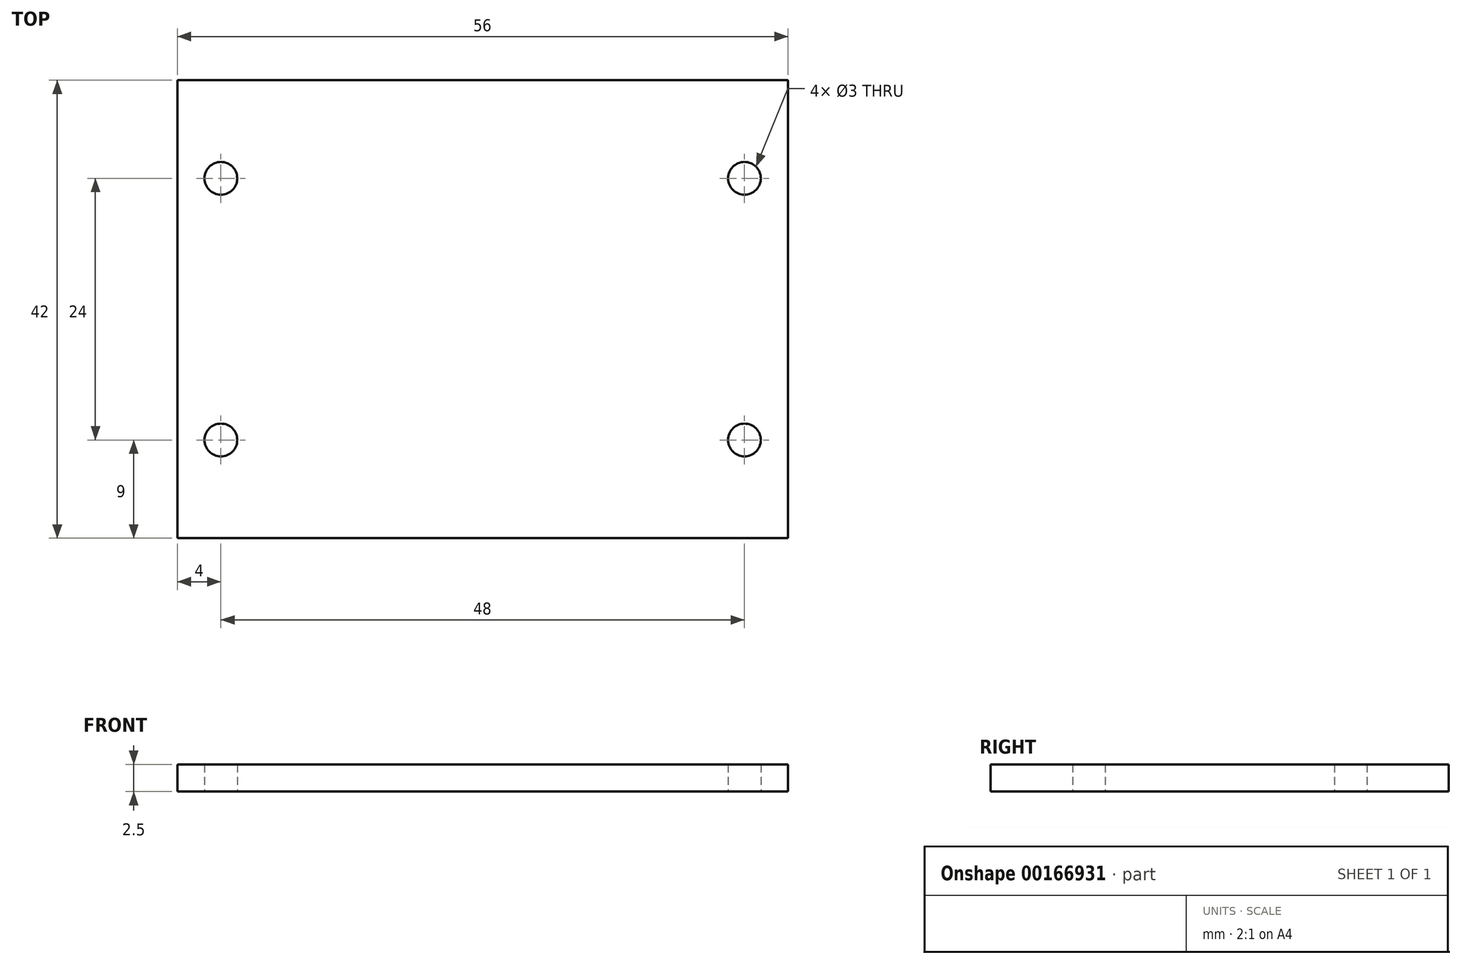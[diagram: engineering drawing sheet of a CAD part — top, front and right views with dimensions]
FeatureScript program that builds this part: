
annotation { "Feature Type Name" : "Feature", "Feature Type Description" : "" }
export const myFeature = defineFeature(function(context is Context, id is Id, definition is map)
    precondition{}
    {
        {
            var Q0;
            Q0=qCreatedBy(makeId("Top.planeOp"),FACE);
            var sketch = newSketch(context, id + "F0", { "sketchPlane" : qUnion([Q0])});
            skLineSegment(sketch, "E0", {"start": v(-28, -21) * mm, "end": v(-28, 21) * mm});
            skLineSegment(sketch, "E1", {"start": v(-28, 21) * mm, "end": v(28, 21) * mm});
            skLineSegment(sketch, "E2", {"start": v(28, 21) * mm, "end": v(28, -21) * mm});
            skLineSegment(sketch, "E3", {"start": v(28, -21) * mm, "end": v(-28, -21) * mm});
            skCircle(sketch, "E4", {"center": v(-24, -12) * mm, "radius": 1.5 * mm});
            skCircle(sketch, "E5", {"center": v(-24, 12) * mm, "radius": 1.5 * mm});
            skCircle(sketch, "E6", {"center": v(24, -12) * mm, "radius": 1.5 * mm});
            skCircle(sketch, "E7", {"center": v(24, 12) * mm, "radius": 1.5 * mm});
            skSolve(sketch);
        }
        {
            var Q0;
            Q0=makeQuery(id+"F0.imprint","IMPRINT",FACE,{"disambiguationData":[TD([[makeQuery(id+"F0.imprint","IMPRINT",EDGE,{"derivedFrom":sQuery(id+"F0.wireOp",EDGE,"E0")}),-1.0]])]});
            extrude(context, id + "F1", {"entities" : qUnion([Q0]), "endBound" : BoundingType.SYMMETRIC, "depth" : 2.5 * mm});
        }
    });
